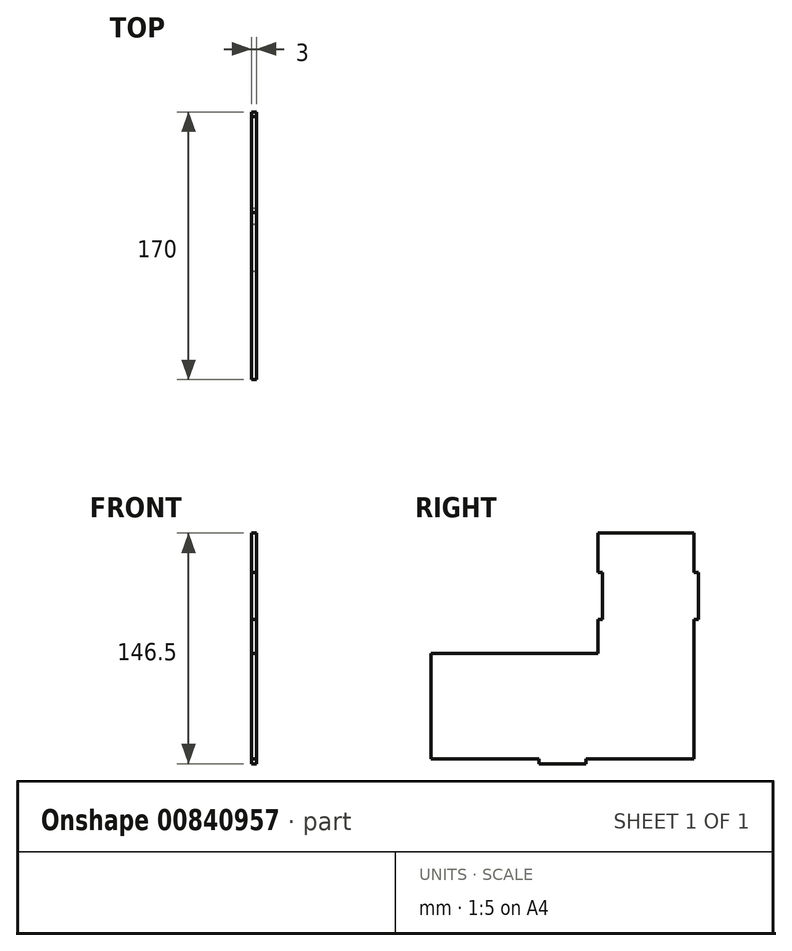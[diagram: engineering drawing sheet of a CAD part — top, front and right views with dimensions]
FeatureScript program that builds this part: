
annotation { "Feature Type Name" : "Feature", "Feature Type Description" : "" }
export const myFeature = defineFeature(function(context is Context, id is Id, definition is map)
    precondition{}
    {
        {
            var Q0;
            Q0=qCreatedBy(makeId("Right.planeOp"),FACE);
            var sketch = newSketch(context, id + "F0", { "sketchPlane" : qUnion([Q0])});
            skLineSegment(sketch, "E0.bottom", {"start": v(0, 0) * mm, "end": v(167, 0) * mm});
            skLineSegment(sketch, "E0.right", {"start": v(167, 0) * mm, "end": v(167, 143.5) * mm});
            skLineSegment(sketch, "E1", {"start": v(167, 143.5) * mm, "end": v(106, 143.5) * mm});
            skLineSegment(sketch, "E2", {"start": v(106, 143.5) * mm, "end": v(106, 67) * mm});
            skLineSegment(sketch, "E3", {"start": v(106, 67) * mm, "end": v(0, 67) * mm});
            skLineSegment(sketch, "E4", {"start": v(0, 67) * mm, "end": v(0, 0) * mm});
            skLineSegment(sketch, "E5", {"start": v(83.5, 0) * mm, "end": v(106, 67) * mm, "construction": true});
            skLineSegment(sketch, "E6.bottom", {"start": v(68.5, 0) * mm, "end": v(98.5, 0) * mm});
            skLineSegment(sketch, "E6.top", {"start": v(68.5, -3) * mm, "end": v(98.5, -3) * mm});
            skLineSegment(sketch, "E6.left", {"start": v(68.5, 0) * mm, "end": v(68.5, -3) * mm});
            skLineSegment(sketch, "E6.right", {"start": v(98.5, 0) * mm, "end": v(98.5, -3) * mm});
            skLineSegment(sketch, "E7.bottom", {"start": v(167, 118.5) * mm, "end": v(170, 118.5) * mm});
            skLineSegment(sketch, "E7.top", {"start": v(167, 88.5) * mm, "end": v(170, 88.5) * mm});
            skLineSegment(sketch, "E7.left", {"start": v(167, 118.5) * mm, "end": v(167, 88.5) * mm});
            skLineSegment(sketch, "E7.right", {"start": v(170, 118.5) * mm, "end": v(170, 88.5) * mm});
            skSolve(sketch);
        }
        {
            var Q0;
            Q0 = qSketchRegion(id + "F0", true);
            extrude(context, id + "F1", {"entities" : qUnion([Q0]), "depth" : 3 * mm, "offsetDistance" : 25 * mm});
        }
        {
            var Q0;
            Q0=makeQuery(id+"F1.opExtrude","CAP_FACE",FACE,{"disambiguationData":[OSD([sQuery(id+"F0.wireOp",EDGE,"E0.bottom"),sQuery(id+"F0.wireOp",EDGE,"E0.right"),sQuery(id+"F0.wireOp",EDGE,"E1"),sQuery(id+"F0.wireOp",EDGE,"E2"),sQuery(id+"F0.wireOp",EDGE,"E3"),sQuery(id+"F0.wireOp",EDGE,"E4"),sQuery(id+"F0.wireOp",EDGE,"E6.top"),sQuery(id+"F0.wireOp",EDGE,"E6.left"),sQuery(id+"F0.wireOp",EDGE,"E6.right"),sQuery(id+"F0.wireOp",EDGE,"E7.bottom"),sQuery(id+"F0.wireOp",EDGE,"E7.top"),sQuery(id+"F0.wireOp",EDGE,"E7.right")])],"isStart":false});
            var sketch = newSketch(context, id + "F2", { "sketchPlane" : qUnion([Q0])});
            skLineSegment(sketch, "E8.bottom", {"start": v(106, 118.5) * mm, "end": v(109, 118.5) * mm});
            skLineSegment(sketch, "E8.top", {"start": v(106, 88.5) * mm, "end": v(109, 88.5) * mm});
            skLineSegment(sketch, "E8.left", {"start": v(106, 118.5) * mm, "end": v(106, 88.5) * mm});
            skLineSegment(sketch, "E8.right", {"start": v(109, 118.5) * mm, "end": v(109, 88.5) * mm});
            skSolve(sketch);
        }
        {
            var Q0;
            Q0 = qSketchRegion(id + "F2", true);
            extrude(context, id + "F3", {"entities" : qUnion([Q0]), "operationType" : NewBodyOperationType.REMOVE, "oppositeDirection" : true, "depth" : 25 * mm, "offsetDistance" : 25 * mm});
        }
    });
